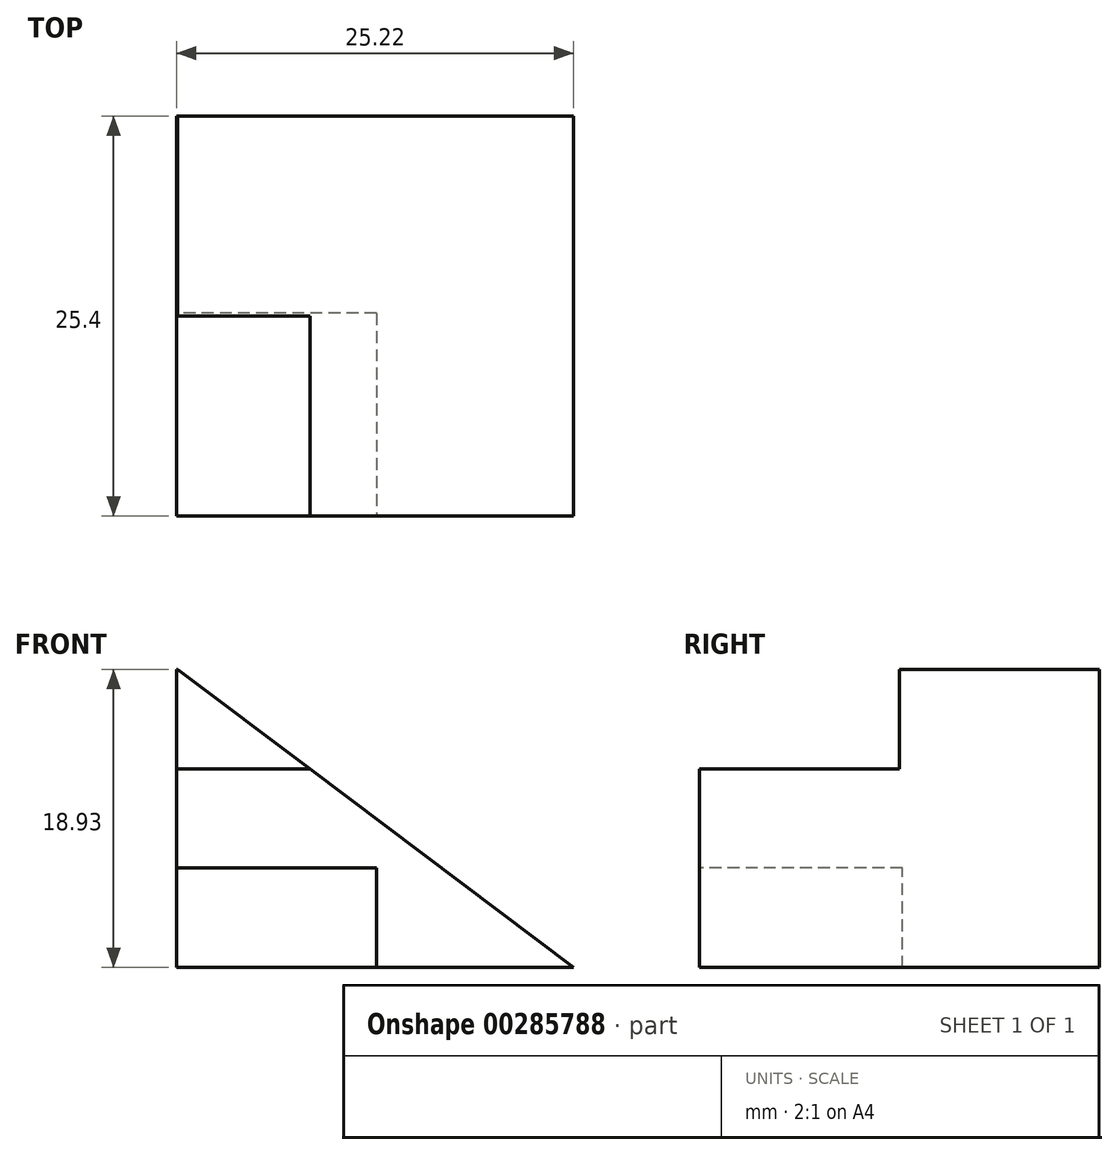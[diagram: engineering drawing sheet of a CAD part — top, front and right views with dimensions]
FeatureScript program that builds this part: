
annotation { "Feature Type Name" : "Feature", "Feature Type Description" : "" }
export const myFeature = defineFeature(function(context is Context, id is Id, definition is map)
    precondition{}
    {
        {
            var Q0;
            Q0=qCreatedBy(makeId("Front.planeOp"),FACE);
            var sketch = newSketch(context, id + "F0", { "sketchPlane" : qUnion([Q0])});
            skLineSegment(sketch, "E0", {"start": v(0, 0) * mm, "end": v(0, 6.35) * mm});
            skLineSegment(sketch, "E1", {"start": v(0, 6.35) * mm, "end": v(25.4, 6.35) * mm});
            skLineSegment(sketch, "E2", {"start": v(25.4, 6.35) * mm, "end": v(25.4, 0) * mm});
            skLineSegment(sketch, "E3", {"start": v(25.4, 0) * mm, "end": v(0, 0) * mm});
            skSolve(sketch);
        }
        {
            var Q0;
            Q0 = qSketchRegion(id + "F0", true);
            extrude(context, id + "F1", {"entities" : qUnion([Q0]), "depth" : 38.1 * mm});
        }
        {
            var Q0;
            Q0=qCreatedBy(makeId("Right.planeOp"),FACE);
            var sketch = newSketch(context, id + "F2", { "sketchPlane" : qUnion([Q0])});
            skLineSegment(sketch, "E4", {"start": v(0, 25.38) * mm, "end": v(-12.7, 25.38) * mm});
            skLineSegment(sketch, "E5", {"start": v(-12.7, 25.38) * mm, "end": v(-12.7, 19.05) * mm});
            skLineSegment(sketch, "E6", {"start": v(-12.7, 19.05) * mm, "end": v(-25.4, 19.05) * mm});
            skLineSegment(sketch, "E7", {"start": v(-25.4, 19.05) * mm, "end": v(-25.4, 6.33) * mm});
            skLineSegment(sketch, "E8", {"start": v(-25.4, 6.33) * mm, "end": v(0, 6.33) * mm});
            skLineSegment(sketch, "E9", {"start": v(0, 6.33) * mm, "end": v(0, 25.38) * mm});
            skLineSegment(sketch, "E10", {"start": v(0, 6.33) * mm, "end": v(-12.7, 6.33) * mm});
            skSolve(sketch);
        }
        {
            var Q0;
            Q0 = qSketchRegion(id + "F2", true);
            extrude(context, id + "F3", {"entities" : qUnion([Q0]), "operationType" : NewBodyOperationType.ADD, "depth" : 25.4 * mm});
        }
        {
            var Q0;
            Q0=qCreatedBy(makeId("Right.planeOp"),FACE);
            var sketch = newSketch(context, id + "F4", { "sketchPlane" : qUnion([Q0])});
            skLineSegment(sketch, "E11", {"start": v(-25.44, 6.41) * mm, "end": v(-12.52, 6.41) * mm});
            skLineSegment(sketch, "E12", {"start": v(-12.52, 6.41) * mm, "end": v(-12.52, 12.76) * mm});
            skLineSegment(sketch, "E13", {"start": v(-12.52, 12.76) * mm, "end": v(-25.44, 12.76) * mm});
            skLineSegment(sketch, "E14", {"start": v(-25.44, 12.76) * mm, "end": v(-25.44, 6.41) * mm});
            skSolve(sketch);
        }
        {
            var Q0;
            Q0 = qSketchRegion(id + "F4", true);
            extrude(context, id + "F5", {"entities" : qUnion([Q0]), "operationType" : NewBodyOperationType.REMOVE, "depth" : 12.7 * mm});
        }
        {
            var Q0;
            Q0=qCreatedBy(makeId("Front.planeOp"),FACE);
            var sketch = newSketch(context, id + "F6", { "sketchPlane" : qUnion([Q0])});
            skLineSegment(sketch, "E15", {"start": v(0, 25.42) * mm, "end": v(25.22, 6.45) * mm});
            skLineSegment(sketch, "E16", {"start": v(25.22, 6.45) * mm, "end": v(0, 6.45) * mm});
            skLineSegment(sketch, "E17", {"start": v(0, 6.45) * mm, "end": v(0, 25.42) * mm});
            skSolve(sketch);
        }
        {
            var Q0;
            Q0 = qSketchRegion(id + "F6", true);
            extrude(context, id + "F7", {"entities" : qUnion([Q0]), "operationType" : NewBodyOperationType.INTERSECT, "depth" : 25.4 * mm});
        }
    });
